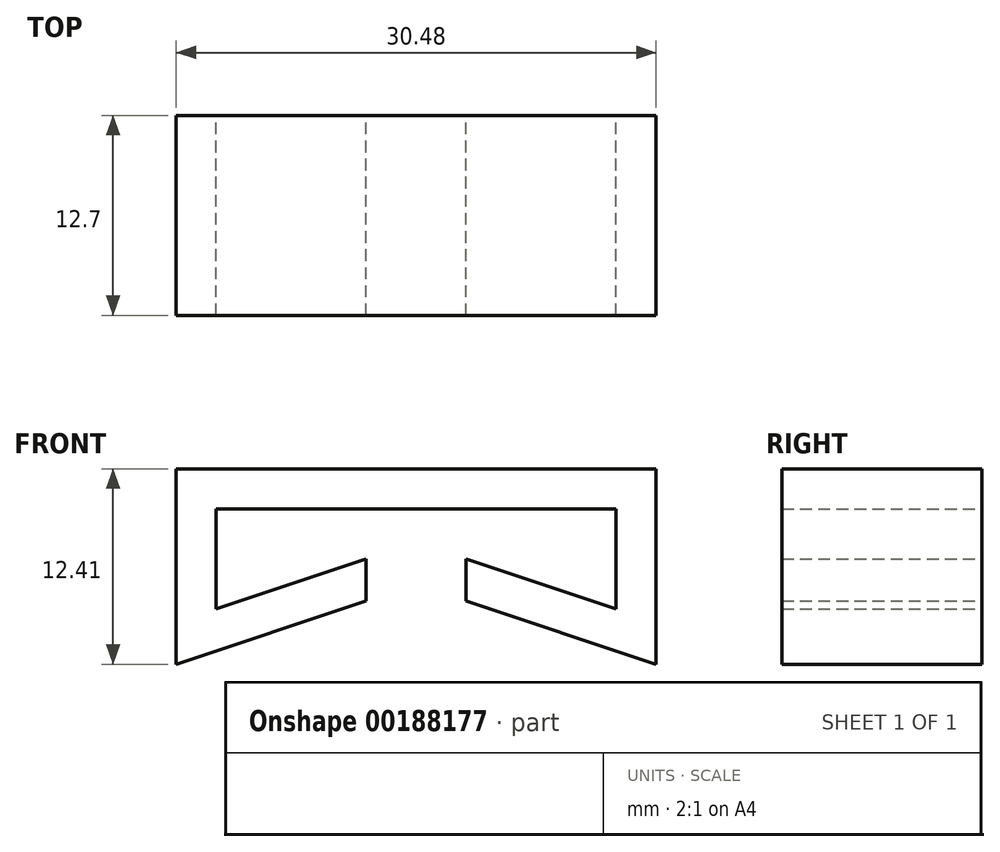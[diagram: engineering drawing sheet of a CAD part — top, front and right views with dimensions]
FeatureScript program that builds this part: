
annotation { "Feature Type Name" : "Feature", "Feature Type Description" : "" }
export const myFeature = defineFeature(function(context is Context, id is Id, definition is map)
    precondition{}
    {
        {
            var Q0;
            Q0=qCreatedBy(makeId("Front.planeOp"),FACE);
            var sketch = newSketch(context, id + "F0", { "sketchPlane" : qUnion([Q0])});
            skLineSegment(sketch, "E0", {"start": v(3.18, -3.17) * mm, "end": v(12.7, -6.35) * mm});
            skLineSegment(sketch, "E1", {"start": v(12.7, -6.35) * mm, "end": v(12.7, 0) * mm});
            skLineSegment(sketch, "E2", {"start": v(12.7, 0) * mm, "end": v(-12.7, 0) * mm});
            skLineSegment(sketch, "E3", {"start": v(-12.7, 0) * mm, "end": v(-12.7, -6.35) * mm});
            skLineSegment(sketch, "E4", {"start": v(-12.7, -6.35) * mm, "end": v(-3.18, -3.18) * mm});
            skLineSegment(sketch, "E5.0", {"start": v(-15.24, -9.87) * mm, "end": v(-3.18, -5.85) * mm});
            skLineSegment(sketch, "E5.1", {"start": v(3.18, -5.85) * mm, "end": v(15.24, -9.87) * mm});
            skLineSegment(sketch, "E5.2", {"start": v(15.24, -9.87) * mm, "end": v(15.24, 2.54) * mm});
            skLineSegment(sketch, "E5.3", {"start": v(15.24, 2.54) * mm, "end": v(-15.24, 2.54) * mm});
            skLineSegment(sketch, "E5.4", {"start": v(-15.24, 2.54) * mm, "end": v(-15.24, -9.87) * mm});
            skLineSegment(sketch, "E6", {"start": v(3.18, -3.17) * mm, "end": v(3.18, -5.85) * mm});
            skLineSegment(sketch, "E7", {"start": v(-3.17, -3.18) * mm, "end": v(-3.17, -5.85) * mm});
            skSolve(sketch);
        }
        {
            var Q0;
            Q0=makeQuery(id+"F0.imprint","IMPRINT",FACE,{"disambiguationData":[TD([[makeQuery(id+"F0.imprint","IMPRINT",EDGE,{"derivedFrom":sQuery(id+"F0.wireOp",EDGE,"E0")}),-1.0]])]});
            extrude(context, id + "F1", {"entities" : qUnion([Q0]), "endBound" : BoundingType.SYMMETRIC, "depth" : 12.7 * mm});
        }
    });
